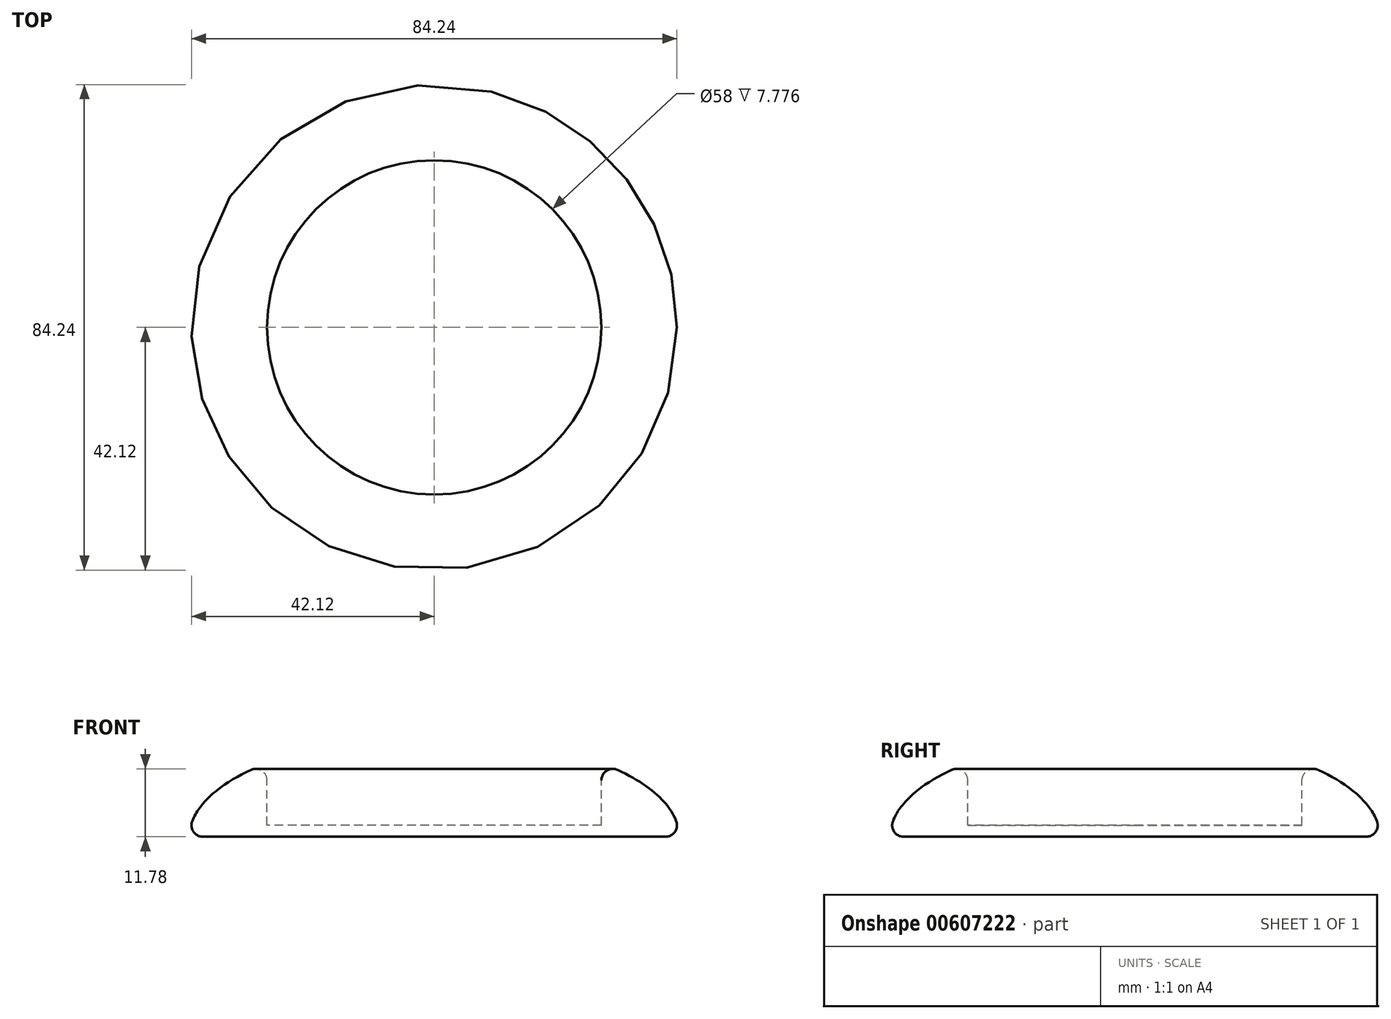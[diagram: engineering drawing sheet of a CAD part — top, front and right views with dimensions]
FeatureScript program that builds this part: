
annotation { "Feature Type Name" : "Feature", "Feature Type Description" : "" }
export const myFeature = defineFeature(function(context is Context, id is Id, definition is map)
    precondition{}
    {
        {
            var Q0;
            Q0=qCreatedBy(makeId("Front.planeOp"),FACE);
            var sketch = newSketch(context, id + "F0", { "sketchPlane" : qUnion([Q0])});
            skEllipticalArc(sketch, "E0", {});
            skLineSegment(sketch, "E1", {"start": v(0, 0) * mm, "end": v(42.5, 0) * mm});
            skLineSegment(sketch, "E2", {"start": v(0, 2) * mm, "end": v(29, 2) * mm});
            skPoint(sketch, "E2.startSnap0", {"position": v(0, 17.5) * mm});
            skLineSegment(sketch, "E3", {"start": v(29, 2) * mm, "end": v(29, 12.8) * mm});
            skPoint(sketch, "E4.orphan", {"position": v(-42.5, 0) * mm});
            skLineSegment(sketch, "E5", {"start": v(0, 2) * mm, "end": v(0, 0) * mm});
            const initialGuessF0  = {"E0": [0, 0, -1, 0, 0.0425, 0.0175, 3.141592653589793, 3.9614124638663384]};
            skSetInitialGuess(sketch, initialGuessF0);
            skSolve(sketch);
        }
        {
            var Q0;
            Q0=makeQuery(id+"F0.imprint","IMPRINT",FACE,{"disambiguationData":[TD([[makeQuery(id+"F0.imprint","IMPRINT",EDGE,{"derivedFrom":sQuery(id+"F0.wireOp",EDGE,"E0")}),1.0]])]});
            var Q1;
            Q1=sQuery(id+"F0.wireOp",EDGE,"E5");
            revolve(context, id + "F1", {"entities" : qUnion([Q0]), "axis" : qUnion([Q1]), "revolveType" : RevolveType.FULL});
        }
        {
            var Q0;
            Q0=makeQuery(id+"F1.opRevolve","SWEPT_EDGE",EDGE,{"disambiguationData":[OSD([sQuery(id+"F0.wireOp",EDGE,"E0"),sQuery(id+"F0.wireOp",EDGE,"E1")])]});
            fillet(context, id + "F2", {"entities" : qUnion([Q0]), "radius" : 2 * mm, "tangentPropagation" : true, "allowEdgeOverflow" : false});
        }
        {
            var Q0;
            Q0=makeQuery(id+"F1.opRevolve","SWEPT_EDGE",EDGE,{"disambiguationData":[OSD([sQuery(id+"F0.wireOp",EDGE,"E0"),sQuery(id+"F0.wireOp",EDGE,"E3")])]});
            fillet(context, id + "F3", {"entities" : qUnion([Q0]), "radius" : 2 * mm, "tangentPropagation" : true, "allowEdgeOverflow" : false});
        }
    });
